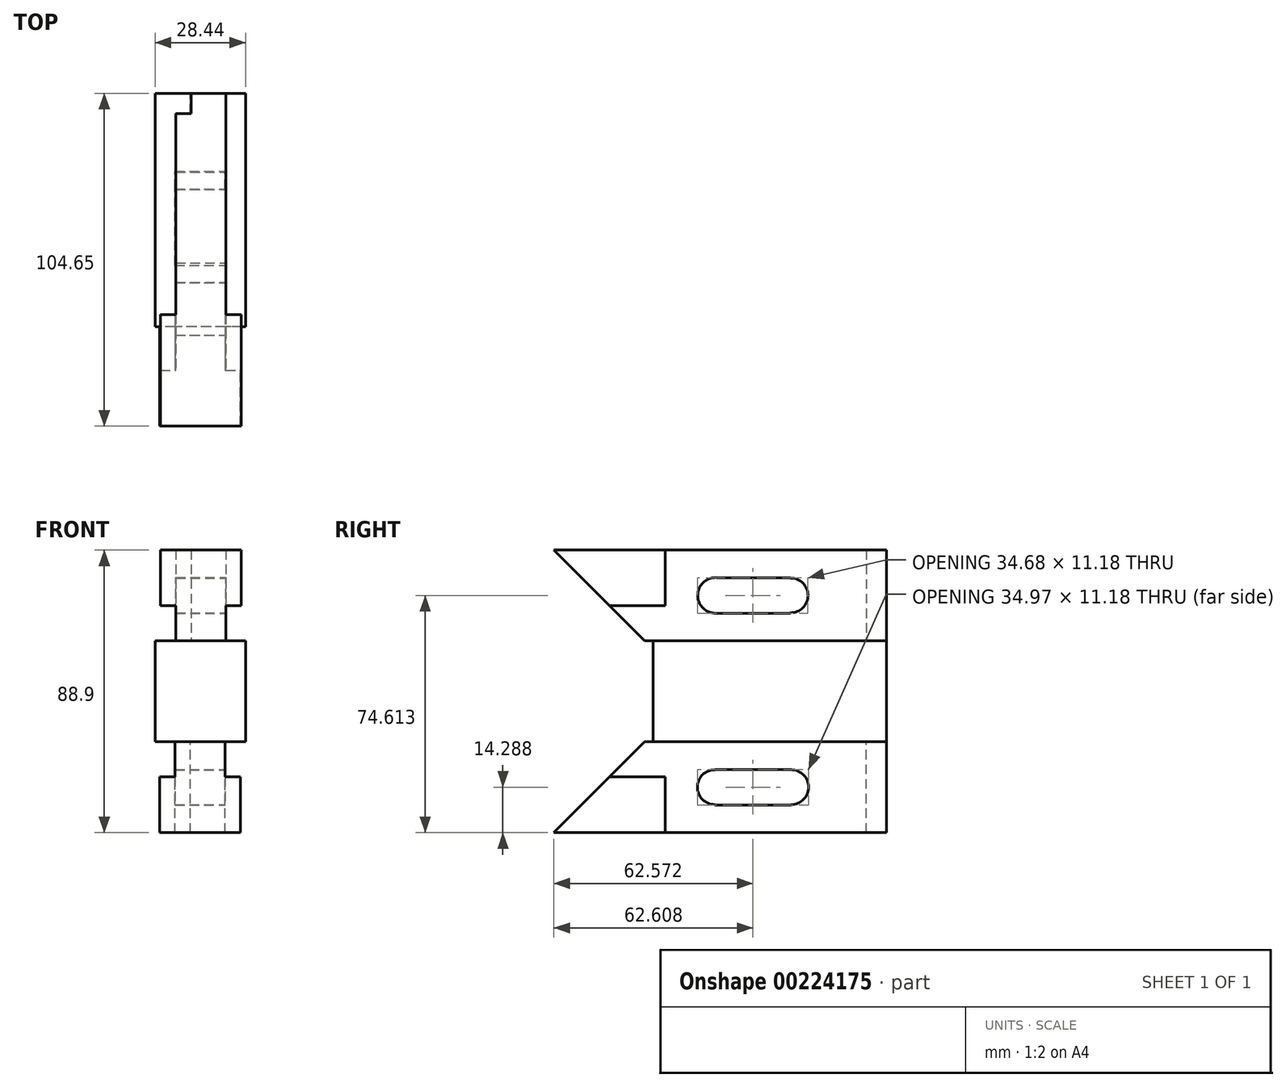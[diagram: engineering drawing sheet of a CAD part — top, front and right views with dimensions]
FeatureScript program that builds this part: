
annotation { "Feature Type Name" : "Feature", "Feature Type Description" : "" }
export const myFeature = defineFeature(function(context is Context, id is Id, definition is map)
    precondition{}
    {
        {
            var Q0;
            Q0=qCreatedBy(makeId("Top.planeOp"),FACE);
            var sketch = newSketch(context, id + "F0", { "sketchPlane" : qUnion([Q0])});
            skLineSegment(sketch, "E0.bottom", {"start": v(14.22, 36.7) * mm, "end": v(-14.22, 36.7) * mm});
            skLineSegment(sketch, "E0.top", {"start": v(14.22, -36.7) * mm, "end": v(-14.22, -36.7) * mm});
            skLineSegment(sketch, "E0.left", {"start": v(14.22, 36.7) * mm, "end": v(14.22, -36.7) * mm});
            skLineSegment(sketch, "E0.right", {"start": v(-14.22, 36.7) * mm, "end": v(-14.22, -36.7) * mm});
            skPoint(sketch, "E0.middle", {"position": v(0, 0) * mm});
            skLineSegment(sketch, "E1", {"start": v(0, 76.3) * mm, "end": v(0, -76.87) * mm, "construction": true});
            skSolve(sketch);
        }
        {
            var Q0;
            Q0=makeQuery(id+"F0.imprint","IMPRINT",FACE,{"disambiguationData":[TD([[makeQuery(id+"F0.imprint","IMPRINT",EDGE,{"derivedFrom":sQuery(id+"F0.wireOp",EDGE,"E0.bottom")}),1.0]])]});
            extrude(context, id + "F1", {"entities" : qUnion([Q0]), "endBound" : BoundingType.SYMMETRIC, "depth" : 31.75 * mm});
        }
        {
            var Q0;
            Q0=makeQuery(id+"F1.opExtrude","CAP_FACE",FACE,{"disambiguationData":[OSD([sQuery(id+"F0.wireOp",EDGE,"E0.bottom"),sQuery(id+"F0.wireOp",EDGE,"E0.top"),sQuery(id+"F0.wireOp",EDGE,"E0.left"),sQuery(id+"F0.wireOp",EDGE,"E0.right")])],"isStart":false});
            var sketch = newSketch(context, id + "F2", { "sketchPlane" : qUnion([Q0])});
            skPoint(sketch, "E2.middle", {"position": v(0, 0) * mm});
            skLineSegment(sketch, "E3.bottom", {"start": v(-7.7, 36.7) * mm, "end": v(8.05, 36.7) * mm});
            skLineSegment(sketch, "E3.top", {"start": v(-7.7, -32.9) * mm, "end": v(8.05, -32.9) * mm});
            skLineSegment(sketch, "E3.left", {"start": v(-7.7, 36.7) * mm, "end": v(-7.7, -32.9) * mm});
            skLineSegment(sketch, "E3.right", {"start": v(8.05, 36.7) * mm, "end": v(8.05, -32.9) * mm});
            skLineSegment(sketch, "E4", {"start": v(-7.7, 30.35) * mm, "end": v(-2.88, 30.35) * mm});
            skLineSegment(sketch, "E5", {"start": v(-2.88, 30.35) * mm, "end": v(-2.88, 36.7) * mm});
            skSolve(sketch);
        }
        {
            var Q0;
            Q0=makeQuery(id+"F1.opExtrude","CAP_FACE",FACE,{"disambiguationData":[OSD([sQuery(id+"F0.wireOp",EDGE,"E0.bottom"),sQuery(id+"F0.wireOp",EDGE,"E0.top"),sQuery(id+"F0.wireOp",EDGE,"E0.left"),sQuery(id+"F0.wireOp",EDGE,"E0.right")])],"isStart":true});
            var sketch = newSketch(context, id + "F3", { "sketchPlane" : qUnion([Q0])});
            skLineSegment(sketch, "E6.bottom", {"start": v(-7.99, -36.7) * mm, "end": v(7.76, -36.7) * mm});
            skLineSegment(sketch, "E6.top", {"start": v(-7.99, 32.9) * mm, "end": v(7.76, 32.9) * mm});
            skLineSegment(sketch, "E6.left", {"start": v(-7.99, -36.7) * mm, "end": v(-7.99, 32.9) * mm});
            skLineSegment(sketch, "E6.right", {"start": v(7.76, -36.7) * mm, "end": v(7.76, 32.9) * mm});
            skLineSegment(sketch, "E7", {"start": v(-7.99, -30.35) * mm, "end": v(-3.16, -30.35) * mm});
            skLineSegment(sketch, "E8", {"start": v(-3.16, -30.35) * mm, "end": v(-3.16, -36.7) * mm});
            skSolve(sketch);
        }
        {
            var Q0;
            {var subQ2=sQuery(id+"F2.wireOp",EDGE,"E3.top");Q0=makeQuery(id+"F2.imprint","IMPRINT",FACE,{"disambiguationData":[TD([[makeQuery(id+"F2.imprint","IMPRINT",EDGE,{"derivedFrom":subQ2}),1.0]])]});}
            extrude(context, id + "F4", {"entities" : qUnion([Q0]), "operationType" : NewBodyOperationType.ADD, "depth" : 28.57 * mm});
        }
        {
            var Q0;
            {var subQ3=sQuery(id+"F3.wireOp",EDGE,"E6.top");Q0=makeQuery(id+"F3.imprint","IMPRINT",FACE,{"disambiguationData":[TD([[makeQuery(id+"F3.imprint","IMPRINT",EDGE,{"derivedFrom":subQ3}),-1.0]])]});}
            extrude(context, id + "F5", {"entities" : qUnion([Q0]), "operationType" : NewBodyOperationType.ADD, "depth" : 28.57 * mm});
        }
        {
            var Q0;
            Q0=makeQuery(id+"F4.opExtrude","CAP_FACE",FACE,{"disambiguationData":[OSD([sQuery(id+"F2.wireOp",EDGE,"E3.bottom"),sQuery(id+"F2.wireOp",EDGE,"E3.top"),sQuery(id+"F2.wireOp",EDGE,"E3.left"),sQuery(id+"F2.wireOp",EDGE,"E3.right"),sQuery(id+"F2.wireOp",EDGE,"E4"),sQuery(id+"F2.wireOp",EDGE,"E5")])],"isStart":false});
            var sketch = newSketch(context, id + "F6", { "sketchPlane" : qUnion([Q0])});
            skLineSegment(sketch, "E9", {"start": v(0.17, -32.9) * mm, "end": v(-12.53, -32.9) * mm, "construction": true});
            skLineSegment(sketch, "E10", {"start": v(0.17, -32.9) * mm, "end": v(12.87, -32.9) * mm, "construction": true});
            skLineSegment(sketch, "E11.bottom", {"start": v(-12.53, -32.9) * mm, "end": v(12.87, -32.9) * mm});
            skLineSegment(sketch, "E11.top", {"start": v(-12.53, -67.95) * mm, "end": v(12.87, -67.95) * mm});
            skLineSegment(sketch, "E11.left", {"start": v(-12.53, -32.9) * mm, "end": v(-12.53, -67.95) * mm});
            skLineSegment(sketch, "E11.right", {"start": v(12.87, -32.9) * mm, "end": v(12.87, -67.95) * mm});
            skSolve(sketch);
        }
        {
            var Q0;
            Q0=makeQuery(id+"F6.imprint","IMPRINT",FACE,{"disambiguationData":[TD([[makeQuery(id+"F6.imprint","IMPRINT",EDGE,{"derivedFrom":sQuery(id+"F6.wireOp",EDGE,"E11.top")}),1.0]])]});
            extrude(context, id + "F7", {"entities" : qUnion([Q0]), "operationType" : NewBodyOperationType.ADD, "oppositeDirection" : true, "depth" : 17.53 * mm});
        }
        {
            var Q0;
            Q0=makeQuery(id+"F5.opExtrude","CAP_FACE",FACE,{"disambiguationData":[OSD([sQuery(id+"F3.wireOp",EDGE,"E6.bottom"),sQuery(id+"F3.wireOp",EDGE,"E6.top"),sQuery(id+"F3.wireOp",EDGE,"E6.left"),sQuery(id+"F3.wireOp",EDGE,"E6.right"),sQuery(id+"F3.wireOp",EDGE,"E7"),sQuery(id+"F3.wireOp",EDGE,"E8")])],"isStart":false});
            var sketch = newSketch(context, id + "F8", { "sketchPlane" : qUnion([Q0])});
            skLineSegment(sketch, "E12", {"start": v(-0.11, 32.9) * mm, "end": v(-12.81, 32.9) * mm, "construction": true});
            skLineSegment(sketch, "E13", {"start": v(-0.11, 32.9) * mm, "end": v(12.59, 32.9) * mm, "construction": true});
            skLineSegment(sketch, "E14.bottom", {"start": v(-12.81, 32.9) * mm, "end": v(12.59, 32.9) * mm});
            skLineSegment(sketch, "E14.top", {"start": v(-12.81, 67.95) * mm, "end": v(12.59, 67.95) * mm});
            skLineSegment(sketch, "E14.left", {"start": v(-12.81, 32.9) * mm, "end": v(-12.81, 67.95) * mm});
            skLineSegment(sketch, "E14.right", {"start": v(12.59, 32.9) * mm, "end": v(12.59, 67.95) * mm});
            skSolve(sketch);
        }
        {
            var Q0;
            Q0=makeQuery(id+"F8.imprint","IMPRINT",FACE,{"disambiguationData":[TD([[makeQuery(id+"F8.imprint","IMPRINT",EDGE,{"derivedFrom":sQuery(id+"F8.wireOp",EDGE,"E14.top")}),-1.0]])]});
            extrude(context, id + "F9", {"entities" : qUnion([Q0]), "operationType" : NewBodyOperationType.ADD, "oppositeDirection" : true, "depth" : 17.53 * mm});
        }
        {
            var Q0;
            Q0=makeQuery(id+"F7.boolean.opBoolean","MERGE",FACE,{"derivedFrom":[makeQuery(id+"F4.opExtrude","CAP_FACE",FACE,{"disambiguationData":[OSD([sQuery(id+"F2.wireOp",EDGE,"E3.bottom"),sQuery(id+"F2.wireOp",EDGE,"E3.top"),sQuery(id+"F2.wireOp",EDGE,"E3.left"),sQuery(id+"F2.wireOp",EDGE,"E3.right"),sQuery(id+"F2.wireOp",EDGE,"E4"),sQuery(id+"F2.wireOp",EDGE,"E5")])],"isStart":false}),makeQuery(id+"F7.opExtrude","CAP_FACE",FACE,{"disambiguationData":[OSD([sQuery(id+"F6.wireOp",EDGE,"E11.bottom"),sQuery(id+"F6.wireOp",EDGE,"E11.top"),sQuery(id+"F6.wireOp",EDGE,"E11.left"),sQuery(id+"F6.wireOp",EDGE,"E11.right")])],"isStart":true})]});
            var sketch = newSketch(context, id + "F10", { "sketchPlane" : qUnion([Q0])});
            skLineSegment(sketch, "E15.bottom", {"start": v(-7.7, -32.9) * mm, "end": v(8.05, -32.9) * mm});
            skLineSegment(sketch, "E15.top", {"start": v(-7.7, -67.95) * mm, "end": v(8.05, -67.95) * mm});
            skLineSegment(sketch, "E15.left", {"start": v(-7.7, -32.9) * mm, "end": v(-7.7, -67.95) * mm});
            skLineSegment(sketch, "E15.right", {"start": v(8.05, -32.9) * mm, "end": v(8.05, -67.95) * mm});
            skSolve(sketch);
        }
        {
            var Q0;
            Q0=makeQuery(id+"F10.imprint","IMPRINT",FACE,{"disambiguationData":[TD([[makeQuery(id+"F10.imprint","IMPRINT",EDGE,{"derivedFrom":sQuery(id+"F10.wireOp",EDGE,"E15.bottom")}),-1.0]])]});
            extrude(context, id + "F11", {"entities" : qUnion([Q0]), "operationType" : NewBodyOperationType.ADD, "oppositeDirection" : true, "depth" : 28.57 * mm});
        }
        {
            var Q0;
            Q0=makeQuery(id+"F9.boolean.opBoolean","MERGE",FACE,{"derivedFrom":[makeQuery(id+"F5.opExtrude","CAP_FACE",FACE,{"disambiguationData":[OSD([sQuery(id+"F3.wireOp",EDGE,"E6.bottom"),sQuery(id+"F3.wireOp",EDGE,"E6.top"),sQuery(id+"F3.wireOp",EDGE,"E6.left"),sQuery(id+"F3.wireOp",EDGE,"E6.right"),sQuery(id+"F3.wireOp",EDGE,"E7"),sQuery(id+"F3.wireOp",EDGE,"E8")])],"isStart":false}),makeQuery(id+"F9.opExtrude","CAP_FACE",FACE,{"disambiguationData":[OSD([sQuery(id+"F8.wireOp",EDGE,"E14.bottom"),sQuery(id+"F8.wireOp",EDGE,"E14.top"),sQuery(id+"F8.wireOp",EDGE,"E14.left"),sQuery(id+"F8.wireOp",EDGE,"E14.right")])],"isStart":true})]});
            var sketch = newSketch(context, id + "F12", { "sketchPlane" : qUnion([Q0])});
            skLineSegment(sketch, "E16.bottom", {"start": v(-7.99, 32.9) * mm, "end": v(7.76, 32.9) * mm});
            skLineSegment(sketch, "E16.top", {"start": v(-7.99, 67.95) * mm, "end": v(7.76, 67.95) * mm});
            skLineSegment(sketch, "E16.left", {"start": v(-7.99, 32.9) * mm, "end": v(-7.99, 67.95) * mm});
            skLineSegment(sketch, "E16.right", {"start": v(7.76, 32.9) * mm, "end": v(7.76, 67.95) * mm});
            skSolve(sketch);
        }
        {
            var Q0;
            Q0=makeQuery(id+"F12.imprint","IMPRINT",FACE,{"disambiguationData":[TD([[makeQuery(id+"F12.imprint","IMPRINT",EDGE,{"derivedFrom":sQuery(id+"F12.wireOp",EDGE,"E16.bottom")}),1.0]])]});
            extrude(context, id + "F13", {"entities" : qUnion([Q0]), "operationType" : NewBodyOperationType.ADD, "oppositeDirection" : true, "depth" : 28.57 * mm});
        }
        {
            var Q0;
            Q0=makeQuery(id+"F7.opExtrude","SWEPT_FACE",FACE,{"disambiguationData":[OSD([sQuery(id+"F6.wireOp",EDGE,"E11.right")])]});
            var sketch = newSketch(context, id + "F14", { "sketchPlane" : qUnion([Q0])});
            skLineSegment(sketch, "E17.bottom", {"start": v(-67.95, 44.45) * mm, "end": v(-39.37, 44.45) * mm});
            skLineSegment(sketch, "E17.top", {"start": v(-67.95, 15.88) * mm, "end": v(-39.37, 15.88) * mm});
            skLineSegment(sketch, "E17.left", {"start": v(-67.95, 44.45) * mm, "end": v(-67.95, 15.88) * mm});
            skLineSegment(sketch, "E17.right", {"start": v(-39.37, 44.45) * mm, "end": v(-39.37, 15.88) * mm});
            skLineSegment(sketch, "E18", {"start": v(-67.95, 44.45) * mm, "end": v(-39.37, 15.88) * mm});
            skSolve(sketch);
        }
        {
            var Q0;
            {var subQ0=sQuery(id+"F14.wireOp",EDGE,"E17.top");Q0=makeQuery(id+"F14.imprint","IMPRINT",FACE,{"disambiguationData":[TD([[makeQuery(id+"F14.imprint","IMPRINT",EDGE,{"derivedFrom":subQ0}),1.0]])]});}
            var Q1;
            {var subQ1=sQuery(id+"F14.wireOp",EDGE,"E17.left");var subQ3=makeQuery(id+"F7.opExtrude","CAP_EDGE",EDGE,{"disambiguationData":[OSD([sQuery(id+"F6.wireOp",EDGE,"E11.right")])],"isStart":false});var subQ4=makeQuery(id+"F14.imprint","INTERSECT",VERTEX,{"derivedFrom":[subQ3,subQ1]});Q1=makeQuery(id+"F14.imprint","IMPRINT",FACE,{"disambiguationData":[TD([[makeQuery(id+"F14.imprint","IMPRINT",EDGE,{"disambiguationData":[TD([[subQ4,1.0]])],"derivedFrom":subQ3}),-1.0]])]});}
            extrude(context, id + "F15", {"entities" : qUnion([Q0, Q1]), "operationType" : NewBodyOperationType.REMOVE, "endBound" : BoundingType.THROUGH_ALL, "oppositeDirection" : true, "depth" : 25.4 * mm});
        }
        {
            var Q0;
            Q0=makeQuery(id+"F9.opExtrude","SWEPT_FACE",FACE,{"disambiguationData":[OSD([sQuery(id+"F8.wireOp",EDGE,"E14.right")])]});
            var sketch = newSketch(context, id + "F16", { "sketchPlane" : qUnion([Q0])});
            skLineSegment(sketch, "E19.bottom", {"start": v(-67.95, -44.45) * mm, "end": v(-39.37, -44.45) * mm});
            skLineSegment(sketch, "E19.top", {"start": v(-67.95, -15.88) * mm, "end": v(-39.37, -15.88) * mm});
            skLineSegment(sketch, "E19.left", {"start": v(-67.95, -44.45) * mm, "end": v(-67.95, -15.88) * mm});
            skLineSegment(sketch, "E19.right", {"start": v(-39.37, -44.45) * mm, "end": v(-39.37, -15.88) * mm});
            skLineSegment(sketch, "E20", {"start": v(-67.95, -44.45) * mm, "end": v(-39.37, -15.88) * mm});
            skSolve(sketch);
        }
        {
            var Q0;
            {var subQ0=sQuery(id+"F16.wireOp",EDGE,"E19.top");Q0=makeQuery(id+"F16.imprint","IMPRINT",FACE,{"disambiguationData":[TD([[makeQuery(id+"F16.imprint","IMPRINT",EDGE,{"derivedFrom":subQ0}),-1.0]])]});}
            var Q1;
            {var subQ1=sQuery(id+"F16.wireOp",EDGE,"E19.left");var subQ3=makeQuery(id+"F9.opExtrude","CAP_EDGE",EDGE,{"disambiguationData":[OSD([sQuery(id+"F8.wireOp",EDGE,"E14.right")])],"isStart":false});var subQ4=makeQuery(id+"F16.imprint","INTERSECT",VERTEX,{"derivedFrom":[subQ3,subQ1]});Q1=makeQuery(id+"F16.imprint","IMPRINT",FACE,{"disambiguationData":[TD([[makeQuery(id+"F16.imprint","IMPRINT",EDGE,{"disambiguationData":[TD([[subQ4,1.0]])],"derivedFrom":subQ3}),1.0]])]});}
            extrude(context, id + "F17", {"entities" : qUnion([Q0, Q1]), "operationType" : NewBodyOperationType.REMOVE, "oppositeDirection" : true, "depth" : 25.4 * mm});
        }
        {
            var Q0;
            Q0=makeQuery(id+"F11.boolean.opBoolean","MERGE",FACE,{"derivedFrom":[makeQuery(id+"F4.opExtrude","SWEPT_FACE",FACE,{"disambiguationData":[OSD([sQuery(id+"F2.wireOp",EDGE,"E3.right")])]}),makeQuery(id+"F11.opExtrude","SWEPT_FACE",FACE,{"disambiguationData":[OSD([sQuery(id+"F10.wireOp",EDGE,"E15.right")])]})]});
            var sketch = newSketch(context, id + "F18", { "sketchPlane" : qUnion([Q0])});
            skLineSegment(sketch, "E21", {"start": v(36.7, 30.16) * mm, "end": v(-47.33, 30.16) * mm, "construction": true});
            skLineSegment(sketch, "E22", {"start": v(36.7, 44.45) * mm, "end": v(12.07, 44.45) * mm, "construction": true});
            skLineSegment(sketch, "E23", {"start": v(12.07, 44.45) * mm, "end": v(12.07, 30.16) * mm, "construction": true});
            skLineSegment(sketch, "E24.bottom", {"start": v(-17.1, 24.57) * mm, "end": v(6.49, 24.57) * mm});
            skLineSegment(sketch, "E24.top", {"start": v(-17.1, 35.75) * mm, "end": v(6.49, 35.75) * mm});
            skLineSegment(sketch, "E24.left", {"start": v(-17.1, 24.57) * mm, "end": v(-17.1, 35.75) * mm});
            skLineSegment(sketch, "E24.right", {"start": v(6.49, 24.57) * mm, "end": v(6.49, 35.75) * mm});
            skPoint(sketch, "E24.middle", {"position": v(-5.31, 30.16) * mm});
            skCircle(sketch, "E25", {"center": v(6.49, 30.16) * mm, "radius": 5.47 * mm});
            skCircle(sketch, "E26", {"center": v(-17.1, 30.16) * mm, "radius": 5.6 * mm});
            skLineSegment(sketch, "E27", {"start": v(-22.99, 39.88) * mm, "end": v(12.07, 39.88) * mm, "construction": true});
            skLineSegment(sketch, "E28", {"start": v(-22.99, 39.88) * mm, "end": v(-22.99, 11.48) * mm, "construction": true});
            skSolve(sketch);
        }
        {
            var Q0;
            {var subQ0=sQuery(id+"F18.wireOp",EDGE,"E24.left");Q0=makeQuery(id+"F18.imprint","IMPRINT",FACE,{"disambiguationData":[TD([[makeQuery(id+"F18.imprint","IMPRINT",EDGE,{"derivedFrom":subQ0}),1.0]])]});}
            var Q1;
            {var subQ0=sQuery(id+"F18.wireOp",EDGE,"E24.left");Q1=makeQuery(id+"F18.imprint","IMPRINT",FACE,{"disambiguationData":[TD([[makeQuery(id+"F18.imprint","IMPRINT",EDGE,{"derivedFrom":subQ0}),-1.0]])]});}
            var Q2;
            {var subQ0=sQuery(id+"F18.wireOp",EDGE,"E24.right");var subQ7=sQuery(id+"F18.wireOp",EDGE,"E24.bottom");var subQ8=makeQuery(id+"F18.imprint","INTERSECT",VERTEX,{"derivedFrom":[subQ7,subQ0]});Q2=makeQuery(id+"F18.imprint","IMPRINT",FACE,{"disambiguationData":[TD([[makeQuery(id+"F18.imprint","IMPRINT",EDGE,{"disambiguationData":[TD([[subQ8,1.0]])],"derivedFrom":subQ7}),1.0]])]});}
            var Q3;
            {var subQ0=sQuery(id+"F18.wireOp",EDGE,"E25");var subQ1=sQuery(id+"F18.wireOp",EDGE,"E24.right");var subQ2=makeQuery(id+"F18.imprint","INTERSECT",VERTEX,{"disambiguationData":[OD(0.0)],"derivedFrom":[subQ1,subQ0]});Q3=makeQuery(id+"F18.imprint","IMPRINT",FACE,{"disambiguationData":[TD([[makeQuery(id+"F18.imprint","IMPRINT",EDGE,{"disambiguationData":[TD([[subQ2,-1.0]])],"derivedFrom":subQ1}),1.0]])]});}
            var Q4;
            {var subQ0=sQuery(id+"F18.wireOp",EDGE,"E25");var subQ1=sQuery(id+"F18.wireOp",EDGE,"E24.right");var subQ2=makeQuery(id+"F18.imprint","INTERSECT",VERTEX,{"disambiguationData":[OD(0.0)],"derivedFrom":[subQ1,subQ0]});Q4=makeQuery(id+"F18.imprint","IMPRINT",FACE,{"disambiguationData":[TD([[makeQuery(id+"F18.imprint","IMPRINT",EDGE,{"disambiguationData":[TD([[subQ2,-1.0]])],"derivedFrom":subQ1}),-1.0]])]});}
            extrude(context, id + "F19", {"entities" : qUnion([Q0, Q1, Q2, Q3, Q4]), "operationType" : NewBodyOperationType.REMOVE, "oppositeDirection" : true, "depth" : 25.4 * mm});
        }
        {
            var Q0;
            Q0=makeQuery(id+"F13.boolean.opBoolean","MERGE",FACE,{"derivedFrom":[makeQuery(id+"F5.opExtrude","SWEPT_FACE",FACE,{"disambiguationData":[OSD([sQuery(id+"F3.wireOp",EDGE,"E6.right")])]}),makeQuery(id+"F13.opExtrude","SWEPT_FACE",FACE,{"disambiguationData":[OSD([sQuery(id+"F12.wireOp",EDGE,"E16.right")])]})]});
            var sketch = newSketch(context, id + "F20", { "sketchPlane" : qUnion([Q0])});
            skLineSegment(sketch, "E29", {"start": v(36.7, -30.16) * mm, "end": v(-30.29, -30.16) * mm, "construction": true});
            skLineSegment(sketch, "E30", {"start": v(36.7, -44.45) * mm, "end": v(12.07, -44.45) * mm, "construction": true});
            skLineSegment(sketch, "E31", {"start": v(12.07, -44.45) * mm, "end": v(12.07, -30.16) * mm, "construction": true});
            skLineSegment(sketch, "E32", {"start": v(12.07, -44.45) * mm, "end": v(-22.99, -44.45) * mm, "construction": true});
            skLineSegment(sketch, "E33", {"start": v(-22.99, -44.45) * mm, "end": v(-22.99, -30.16) * mm, "construction": true});
            skLineSegment(sketch, "E34.bottom", {"start": v(6.66, -35.75) * mm, "end": v(-17.36, -35.75) * mm});
            skLineSegment(sketch, "E34.top", {"start": v(6.66, -24.57) * mm, "end": v(-17.36, -24.57) * mm});
            skLineSegment(sketch, "E34.left", {"start": v(6.66, -35.75) * mm, "end": v(6.66, -24.57) * mm});
            skLineSegment(sketch, "E34.right", {"start": v(-17.36, -35.75) * mm, "end": v(-17.36, -24.57) * mm});
            skPoint(sketch, "E34.middle", {"position": v(-5.35, -30.16) * mm});
            skCircle(sketch, "E35", {"center": v(6.66, -30.16) * mm, "radius": 5.48 * mm});
            skCircle(sketch, "E36", {"center": v(-17.36, -30.16) * mm, "radius": 5.47 * mm});
            skSolve(sketch);
        }
        {
            var Q0;
            {var subQ0=sQuery(id+"F20.wireOp",EDGE,"E36");var subQ1=sQuery(id+"F20.wireOp",EDGE,"E34.right");var subQ2=makeQuery(id+"F20.imprint","INTERSECT",VERTEX,{"disambiguationData":[OD(0.0)],"derivedFrom":[subQ1,subQ0]});Q0=makeQuery(id+"F20.imprint","IMPRINT",FACE,{"disambiguationData":[TD([[makeQuery(id+"F20.imprint","IMPRINT",EDGE,{"disambiguationData":[TD([[subQ2,-1.0]])],"derivedFrom":subQ1}),1.0]])]});}
            var Q1;
            {var subQ0=sQuery(id+"F20.wireOp",EDGE,"E36");var subQ1=sQuery(id+"F20.wireOp",EDGE,"E34.right");var subQ2=makeQuery(id+"F20.imprint","INTERSECT",VERTEX,{"disambiguationData":[OD(0.0)],"derivedFrom":[subQ1,subQ0]});Q1=makeQuery(id+"F20.imprint","IMPRINT",FACE,{"disambiguationData":[TD([[makeQuery(id+"F20.imprint","IMPRINT",EDGE,{"disambiguationData":[TD([[subQ2,-1.0]])],"derivedFrom":subQ1}),-1.0]])]});}
            var Q2;
            {var subQ4=sQuery(id+"F20.wireOp",EDGE,"E34.bottom");Q2=makeQuery(id+"F20.imprint","IMPRINT",FACE,{"disambiguationData":[TD([[makeQuery(id+"F20.imprint","IMPRINT",EDGE,{"derivedFrom":subQ4}),-1.0]])]});}
            var Q3;
            {var subQ0=sQuery(id+"F20.wireOp",EDGE,"E35");var subQ1=sQuery(id+"F20.wireOp",EDGE,"E34.left");var subQ2=makeQuery(id+"F20.imprint","INTERSECT",VERTEX,{"disambiguationData":[OD(0.0)],"derivedFrom":[subQ1,subQ0]});Q3=makeQuery(id+"F20.imprint","IMPRINT",FACE,{"disambiguationData":[TD([[makeQuery(id+"F20.imprint","IMPRINT",EDGE,{"disambiguationData":[TD([[subQ2,-1.0]])],"derivedFrom":subQ1}),1.0]])]});}
            var Q4;
            {var subQ0=sQuery(id+"F20.wireOp",EDGE,"E35");var subQ1=sQuery(id+"F20.wireOp",EDGE,"E34.left");var subQ2=makeQuery(id+"F20.imprint","INTERSECT",VERTEX,{"disambiguationData":[OD(0.0)],"derivedFrom":[subQ1,subQ0]});Q4=makeQuery(id+"F20.imprint","IMPRINT",FACE,{"disambiguationData":[TD([[makeQuery(id+"F20.imprint","IMPRINT",EDGE,{"disambiguationData":[TD([[subQ2,-1.0]])],"derivedFrom":subQ1}),-1.0]])]});}
            extrude(context, id + "F21", {"entities" : qUnion([Q0, Q1, Q2, Q3, Q4]), "operationType" : NewBodyOperationType.REMOVE, "oppositeDirection" : true, "depth" : 25.4 * mm});
        }
    });
